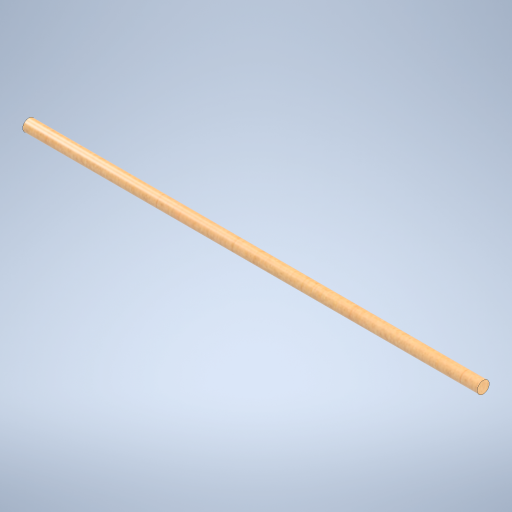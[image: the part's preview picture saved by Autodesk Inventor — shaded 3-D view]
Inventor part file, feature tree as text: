
AUTODESK INVENTOR PART (.ipt)
format: ipt  version: 2023 (Build 270158000, 158)  size: 265,216 bytes
history: native  units: mm
features: extrude x1, plane x1, sketch x1
ambient origin geometry x8: Origin, YZ Plane, XZ Plane, XY Plane, X Axis, Y Axis, Z Axis, Center Point
bodies: Volumenkörper1 (feature_tree)
feature tree (3):
  extrude  "Extrusion1"  Depth=380.0mm TaperAngle=0.0deg
  plane  "Arbeitsebene1"
  sketch  "Skizze1"  dims[d0=10.0mm d1=380.0mm d2=0.0mm d3=0.0mm]
